# Revit family: Thorn CHAMPION
name_source: partatom
category: Lighting Fixtures
revit_build: Autodesk Revit 2016 (Build: 20150220_1215(x64)
units: mm (PartAtom-declared; Revit-internal decimal feet)

## family parameters
Cut with Voids When Loaded = No
Host = Face
Light Source = Yes
OmniClass Number = 23.80.70.11
OmniClass Title = Luminaries for Internal Lighting
Part Type = Normal
Room Calculation Point = No
Round Connector Dimension = Use Diameter
Shared = No

## types (4) — shared parameters
Apparent Load = 939 VA
Assembly Code = D5020200
Color Filter = 16777215
Description = LED flootlight
Dimming Lamp Color Temperature Shift = <None>
Lamp = LED
Length = 707 mm
Manufacturer = Thorn Lighting
Tilt Angle = 0.00°
URL = http://www.thornlighting.com
Voltage = 230 V
zero-valued in all types: Default Elevation

## per-type parameters (varying)
| type | Height | Model | Photometric Web File | Width |
| CHAMPION 264L-740 V2 VSR ANT | 309 mm  [stored 1.01378 ft] | 96633216 | 96633216_(1200mA).IES | 692 mm  [stored 2.27034 ft] |
| CHAMPION 264L-740 V1 VSP ANT | 315 mm  [stored 1.03346 ft] | 92917406 | 92917406_(1200mA).IES | 688 mm  [stored 2.25722 ft] |
| CHAMPION 264L-740 V2 VSP ANT | 315 mm  [stored 1.03346 ft] | 96633302 | 96633302_(1200mA).IES | 688 mm  [stored 2.25722 ft] |
| CHAMPION 264L-740 V3 VSP ANT | 315 mm  [stored 1.03346 ft] | 96633301 | 96633301_(1200mA).IES | 694 mm |

note: [stored X ft] marks values corroborated as IEEE doubles in the binary element streams (Revit-internal decimal feet)

## geometry (parser evidence)
native form markers: Sweep x3
no freeform markers — native parametric forms only
